# Revit family: Световые табло_ПРЕСТИЖ
name_source: partatom
category: Системы пожарной сигнализации
revit_build: Autodesk Revit MEP 2016 (Build: 20150220_1215(x64)
units: mm (PartAtom-declared; Revit-internal decimal feet)

## family parameters
Общий = Нет
Основа = Грань
При загрузке вырезать с полостями = Нет
Размер круглого соединителя = Использовать диаметр
Сохранять ориентацию аннотаций = Нет
Тип детали = Нормальный
Точка расчета площади = Нет

## types (2) — shared parameters
ADSK_URL документации изделия = https://omelta.com
ADSK_URL страницы изделия = https://omelta.com
ADSK_Единица измерения = шт.
ADSK_Завод-изготовитель = г. Омск, ООО «Электротехника и Автоматика»
ADSK_Код изделия = 437245
ADSK_Масса = 0.55
ADSK_Наименование = Световое табло
ADSK_Обозначение = Световое табло
ADSK_Размер_Высота = 125 мм
ADSK_Размер_Глубина = 12 мм
ADSK_Размер_Ширина = 322 мм
ADSK_Ток = 40 мА
IP = 41
Гарантийный срок службы = 3 года
Диапазон рабочих температур = –30...+55 °С
Корпус_Отступ_ВерхНиз = 20 мм
Корпус_Отступ_Сбоку = 20 мм
Материал_Корпус = ЭиА_Белый
Материал_Фон = ЭиА_Зеленый
zero-valued in all types: Отметка по умолчанию

## per-type parameters (varying)
| type | ADSK_Напряжение | ADSK_Номинальная мощность |
| ПРЕСТИЖ-12 | 12 В | 0 В·А |
| ПРЕСТИЖ-24 | 24 В | 1 В·А |

note: column(s) folded — value = type name in every type: ADSK_Марка

## geometry (parser evidence)
native form markers: Blend x2
no freeform markers — native parametric forms only
